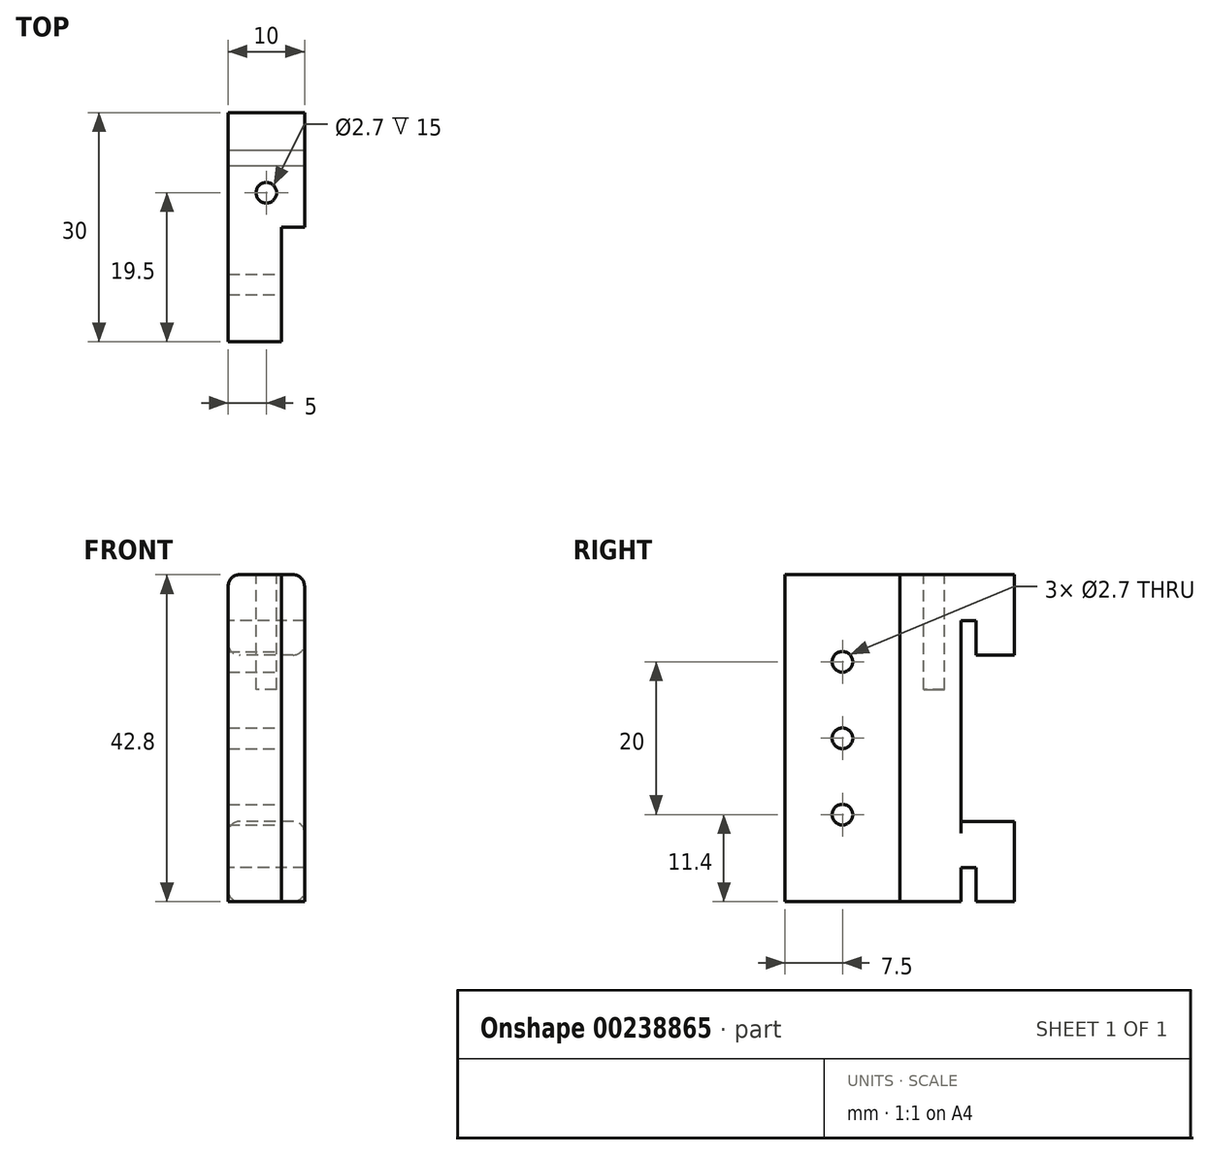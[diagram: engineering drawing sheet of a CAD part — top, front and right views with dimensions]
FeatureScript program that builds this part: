
annotation { "Feature Type Name" : "Feature", "Feature Type Description" : "" }
export const myFeature = defineFeature(function(context is Context, id is Id, definition is map)
    precondition{}
    {
        {
            var Q0;
            Q0=qCreatedBy(makeId("Right.planeOp"),FACE);
            var sketch = newSketch(context, id + "F0", { "sketchPlane" : qUnion([Q0])});
            skLineSegment(sketch, "E0", {"start": v(-23, 0) * mm, "end": v(-23, -42.8) * mm});
            skLineSegment(sketch, "E1", {"start": v(-23, -42.8) * mm, "end": v(0, -42.8) * mm});
            skLineSegment(sketch, "E2", {"start": v(0, -42.8) * mm, "end": v(0, -38.3) * mm});
            skLineSegment(sketch, "E3", {"start": v(0, -38.3) * mm, "end": v(2, -38.3) * mm});
            skLineSegment(sketch, "E4", {"start": v(2, -38.3) * mm, "end": v(2, -42.8) * mm});
            skLineSegment(sketch, "E5", {"start": v(2, -42.8) * mm, "end": v(7, -42.8) * mm});
            skLineSegment(sketch, "E6", {"start": v(7, -42.8) * mm, "end": v(7, -32.3) * mm});
            skLineSegment(sketch, "E7", {"start": v(7, -32.3) * mm, "end": v(0, -32.3) * mm});
            skLineSegment(sketch, "E8", {"start": v(0, -32.3) * mm, "end": v(0, -6) * mm});
            skLineSegment(sketch, "E9", {"start": v(0, -6) * mm, "end": v(2, -6) * mm});
            skLineSegment(sketch, "E10", {"start": v(2, -6) * mm, "end": v(2, -10.5) * mm});
            skLineSegment(sketch, "E11", {"start": v(2, -10.5) * mm, "end": v(7, -10.5) * mm});
            skLineSegment(sketch, "E12", {"start": v(7, -10.5) * mm, "end": v(7, 0) * mm});
            skLineSegment(sketch, "E13", {"start": v(7, 0) * mm, "end": v(-23, 0) * mm});
            skSolve(sketch);
        }
        {
            var Q0;
            Q0 = qSketchRegion(id + "F0", true);
            extrude(context, id + "F1", {"entities" : qUnion([Q0]), "depth" : 10 * mm});
        }
        {
            var Q0;
            Q0=makeQuery(id+"F1.opExtrude","CAP_FACE",FACE,{"disambiguationData":[OSD([sQuery(id+"F0.wireOp",EDGE,"E0"),sQuery(id+"F0.wireOp",EDGE,"E1"),sQuery(id+"F0.wireOp",EDGE,"E2"),sQuery(id+"F0.wireOp",EDGE,"E3"),sQuery(id+"F0.wireOp",EDGE,"E4"),sQuery(id+"F0.wireOp",EDGE,"E5"),sQuery(id+"F0.wireOp",EDGE,"E6"),sQuery(id+"F0.wireOp",EDGE,"E7"),sQuery(id+"F0.wireOp",EDGE,"E8"),sQuery(id+"F0.wireOp",EDGE,"E9"),sQuery(id+"F0.wireOp",EDGE,"E10"),sQuery(id+"F0.wireOp",EDGE,"E11"),sQuery(id+"F0.wireOp",EDGE,"E12"),sQuery(id+"F0.wireOp",EDGE,"E13")])],"isStart":false});
            var sketch = newSketch(context, id + "F2", { "sketchPlane" : qUnion([Q0])});
            skLineSegment(sketch, "E14.bottom", {"start": v(-23, 0) * mm, "end": v(-8, 0) * mm});
            skLineSegment(sketch, "E14.top", {"start": v(-23, -42.8) * mm, "end": v(-8, -42.8) * mm});
            skLineSegment(sketch, "E14.left", {"start": v(-23, 0) * mm, "end": v(-23, -42.8) * mm});
            skLineSegment(sketch, "E14.right", {"start": v(-8, 0) * mm, "end": v(-8, -42.8) * mm});
            skSolve(sketch);
        }
        {
            var Q0;
            Q0 = qSketchRegion(id + "F2", true);
            extrude(context, id + "F3", {"entities" : qUnion([Q0]), "operationType" : NewBodyOperationType.REMOVE, "oppositeDirection" : true, "depth" : 3 * mm});
        }
        {
            var Q0;
            Q0=makeQuery(id+"F3.boolean.opBoolean","COPY",FACE,{"derivedFrom":makeQuery(id+"F3.opExtrude","CAP_FACE",FACE,{"disambiguationData":[OSD([sQuery(id+"F2.wireOp",EDGE,"E14.bottom"),sQuery(id+"F2.wireOp",EDGE,"E14.top"),sQuery(id+"F2.wireOp",EDGE,"E14.left"),sQuery(id+"F2.wireOp",EDGE,"E14.right")])],"isStart":false})});
            var sketch = newSketch(context, id + "F4", { "sketchPlane" : qUnion([Q0])});
            skLineSegment(sketch, "E15", {"start": v(-15.5, 6.41) * mm, "end": v(-15.5, -51.63) * mm, "construction": true});
            skPoint(sketch, "E15.startSnap0", {"position": v(-15.5, 0) * mm});
            skCircle(sketch, "E16", {"center": v(-15.5, -21.4) * mm, "radius": 1.35 * mm});
            skPoint(sketch, "E16.centerSnap0", {"position": v(-23, -21.4) * mm});
            skCircle(sketch, "E17", {"center": v(-15.5, -11.4) * mm, "radius": 1.35 * mm});
            skCircle(sketch, "E18", {"center": v(-15.5, -31.4) * mm, "radius": 1.35 * mm});
            skSolve(sketch);
        }
        {
            var Q0;
            Q0 = qSketchRegion(id + "F4", true);
            extrude(context, id + "F5", {"entities" : qUnion([Q0]), "operationType" : NewBodyOperationType.REMOVE, "endBound" : BoundingType.THROUGH_ALL, "oppositeDirection" : true, "depth" : 25 * mm});
        }
        {
            var Q0;
            Q0=makeQuery(id+"F1.opExtrude","SWEPT_FACE",FACE,{"disambiguationData":[OSD([sQuery(id+"F0.wireOp",EDGE,"E13")])]});
            var sketch = newSketch(context, id + "F6", { "sketchPlane" : qUnion([Q0])});
            skLineSegment(sketch, "E19", {"start": v(5, 9.97) * mm, "end": v(5, -28.7) * mm, "construction": true});
            skPoint(sketch, "E19.startSnap0", {"position": v(5, 7) * mm});
            skCircle(sketch, "E20", {"center": v(5, -3.5) * mm, "radius": 1.35 * mm});
            skSolve(sketch);
        }
        {
            var Q0;
            Q0 = qSketchRegion(id + "F6", true);
            extrude(context, id + "F7", {"entities" : qUnion([Q0]), "operationType" : NewBodyOperationType.REMOVE, "oppositeDirection" : true, "depth" : 15 * mm});
        }
        {
            var Q0;
            Q0=makeQuery(id+"F1.opExtrude","CAP_EDGE",EDGE,{"disambiguationData":[OSD([sQuery(id+"F0.wireOp",EDGE,"E13")])],"isStart":false});
            var Q1;
            Q1=makeQuery(id+"F1.opExtrude","CAP_EDGE",EDGE,{"disambiguationData":[OSD([sQuery(id+"F0.wireOp",EDGE,"E13")])],"isStart":true});
            var Q2;
            Q2=makeQuery(id+"F1.opExtrude","CAP_EDGE",EDGE,{"disambiguationData":[OSD([sQuery(id+"F0.wireOp",EDGE,"E11")])],"isStart":false});
            var Q3;
            Q3=makeQuery(id+"F1.opExtrude","CAP_EDGE",EDGE,{"disambiguationData":[OSD([sQuery(id+"F0.wireOp",EDGE,"E7")])],"isStart":false});
            var Q4;
            Q4=makeQuery(id+"F1.opExtrude","CAP_EDGE",EDGE,{"disambiguationData":[OSD([sQuery(id+"F0.wireOp",EDGE,"E5")])],"isStart":false});
            var Q5;
            Q5=makeQuery(id+"F1.opExtrude","CAP_EDGE",EDGE,{"disambiguationData":[OSD([sQuery(id+"F0.wireOp",EDGE,"E11")])],"isStart":true});
            var Q6;
            Q6=makeQuery(id+"F1.opExtrude","CAP_EDGE",EDGE,{"disambiguationData":[OSD([sQuery(id+"F0.wireOp",EDGE,"E5")])],"isStart":true});
            var Q7;
            Q7=makeQuery(id+"F1.opExtrude","CAP_EDGE",EDGE,{"disambiguationData":[OSD([sQuery(id+"F0.wireOp",EDGE,"E7")])],"isStart":true});
            fillet(context, id + "F8", {"entities" : qUnion([Q0, Q1, Q2, Q3, Q4, Q5, Q6, Q7]), "radius" : 1.5 * mm, "tangentPropagation" : true, "allowEdgeOverflow" : false});
        }
    });
